FCSTD DOCUMENT  (FreeCAD 0.18R4 (GitTag))
Label: Ford_connector
License: All rights reserved
LicenseURL: http://en.wikipedia.org/wiki/All_rights_reserved
objects: Sketcher::SketchObject×1, TechDraw::DrawSVGTemplate×1, TechDraw::DrawViewPart×1, TechDraw::DrawPage×1
note: 1 computed .brp shape members not serialized (recipe doc carries the construction recipe); baked Part::Feature solids carry a one-line shape summary decoded from their .brp

FEATURE [Sketcher::SketchObject] Sketch
  sketch-geometry (120):
    g0: LineSegment StartX=1.5875 StartY=0 StartZ=0 EndX=138.112 EndY=0 EndZ=0
    g1: LineSegment StartX=139.7 StartY=-1.5875 StartZ=0 EndX=139.7 EndY=-163.512 EndZ=0
    g2: LineSegment StartX=138.112 StartY=-165.1 StartZ=0 EndX=1.5875 EndY=-165.1 EndZ=0
    g3: LineSegment StartX=0 StartY=-163.512 StartZ=0 EndX=0 EndY=-1.5875 EndZ=0
    g4: Circle CenterX=6.0198 CenterY=-8.636 CenterZ=0 NormalX=0 NormalY=0 NormalZ=1 AngleXU=0 Radius=3.175
    g5: Circle CenterX=133.68 CenterY=-8.636 CenterZ=0 NormalX=0 NormalY=0 NormalZ=1 AngleXU=0 Radius=3.175
    g6: GeomPoint X=2.8448 Y=-8.636 Z=0
    g7: GeomPoint X=6.0198 Y=-5.461 Z=0
    g8: GeomPoint X=136.855 Y=-8.636 Z=0
    g9: Circle CenterX=21.59 CenterY=-3.175 CenterZ=0 NormalX=0 NormalY=0 NormalZ=1 AngleXU=0 Radius=0.635
    g10: Circle CenterX=22.86 CenterY=-6.35 CenterZ=0 NormalX=0 NormalY=0 NormalZ=1 AngleXU=0 Radius=0.635
    g11: Circle CenterX=24.13 CenterY=-9.525 CenterZ=0 NormalX=0 NormalY=0 NormalZ=1 AngleXU=0 Radius=0.635
    g12: GeomPoint X=21.59 Y=-2.54 Z=0
    g13: GeomPoint X=22.225 Y=-3.175 Z=0
    g14: GeomPoint X=22.86 Y=-5.715 Z=0
    g15: GeomPoint X=22.225 Y=-6.35 Z=0
    g16: GeomPoint X=24.13 Y=-8.89 Z=0
    g17: GeomPoint X=23.495 Y=-9.525 Z=0
    g18: LineSegment StartX=21.59 StartY=-3.175 StartZ=0 EndX=25.908 EndY=-3.18045 EndZ=0
    g19: Circle CenterX=28.448 CenterY=-9.53045 CenterZ=0 NormalX=0 NormalY=0 NormalZ=1 AngleXU=0 Radius=0.635
    g20: Circle CenterX=27.1866 CenterY=-6.35545 CenterZ=0 NormalX=0 NormalY=0 NormalZ=1 AngleXU=0 Radius=0.635
    g21: Circle CenterX=25.908 CenterY=-3.18045 CenterZ=0 NormalX=0 NormalY=0 NormalZ=1 AngleXU=0 Radius=0.635
    g22: LineSegment [constr] StartX=24.13 StartY=-9.525 StartZ=0 EndX=28.448 EndY=-9.53045 EndZ=0
    g23: Circle CenterX=32.766 CenterY=-9.5359 CenterZ=0 NormalX=0 NormalY=0 NormalZ=1 AngleXU=0 Radius=0.635
    g24: Circle CenterX=31.5133 CenterY=-6.3609 CenterZ=0 NormalX=0 NormalY=0 NormalZ=1 AngleXU=0 Radius=0.635
    g25: Circle CenterX=30.2433 CenterY=-3.1859 CenterZ=0 NormalX=0 NormalY=0 NormalZ=1 AngleXU=0 Radius=0.635
    g26: LineSegment [constr] StartX=28.448 StartY=-9.53045 StartZ=0 EndX=32.766 EndY=-9.5359 EndZ=0
    g27: Circle CenterX=37.084 CenterY=-9.54134 CenterZ=0 NormalX=0 NormalY=0 NormalZ=1 AngleXU=0 Radius=0.635
    g28: Circle CenterX=35.8399 CenterY=-6.36634 CenterZ=0 NormalX=0 NormalY=0 NormalZ=1 AngleXU=0 Radius=0.635
    g29: Circle CenterX=34.5699 CenterY=-3.19134 CenterZ=0 NormalX=0 NormalY=0 NormalZ=1 AngleXU=0 Radius=0.635
    g30: LineSegment [constr] StartX=32.766 StartY=-9.5359 StartZ=0 EndX=37.084 EndY=-9.54134 EndZ=0
    g31: Circle CenterX=41.402 CenterY=-9.54679 CenterZ=0 NormalX=0 NormalY=0 NormalZ=1 AngleXU=0 Radius=0.635
    g32: Circle CenterX=40.1665 CenterY=-6.37179 CenterZ=0 NormalX=0 NormalY=0 NormalZ=1 AngleXU=0 Radius=0.635
    g33: Circle CenterX=38.8965 CenterY=-3.19679 CenterZ=0 NormalX=0 NormalY=0 NormalZ=1 AngleXU=0 Radius=0.635
    g34: LineSegment [constr] StartX=37.084 StartY=-9.54134 StartZ=0 EndX=41.402 EndY=-9.54679 EndZ=0
    g35: Circle CenterX=45.72 CenterY=-9.55224 CenterZ=0 NormalX=0 NormalY=0 NormalZ=1 AngleXU=0 Radius=0.635
    g36: Circle CenterX=44.4931 CenterY=-6.37724 CenterZ=0 NormalX=0 NormalY=0 NormalZ=1 AngleXU=0 Radius=0.635
    g37: Circle CenterX=43.2232 CenterY=-3.20224 CenterZ=0 NormalX=0 NormalY=0 NormalZ=1 AngleXU=0 Radius=0.635
    g38: LineSegment [constr] StartX=41.402 StartY=-9.54679 StartZ=0 EndX=45.72 EndY=-9.55224 EndZ=0
    g39: Circle CenterX=50.038 CenterY=-9.55769 CenterZ=0 NormalX=0 NormalY=0 NormalZ=1 AngleXU=0 Radius=0.635
    g40: Circle CenterX=48.8198 CenterY=-6.38269 CenterZ=0 NormalX=0 NormalY=0 NormalZ=1 AngleXU=0 Radius=0.635
    g41: Circle CenterX=47.5498 CenterY=-3.20769 CenterZ=0 NormalX=0 NormalY=0 NormalZ=1 AngleXU=0 Radius=0.635
    g42: LineSegment [constr] StartX=45.72 StartY=-9.55224 StartZ=0 EndX=50.038 EndY=-9.55769 EndZ=0
    g43: Circle CenterX=54.356 CenterY=-9.56314 CenterZ=0 NormalX=0 NormalY=0 NormalZ=1 AngleXU=0 Radius=0.635
    g44: Circle CenterX=53.1464 CenterY=-6.38814 CenterZ=0 NormalX=0 NormalY=0 NormalZ=1 AngleXU=0 Radius=0.635
    g45: Circle CenterX=51.8764 CenterY=-3.21314 CenterZ=0 NormalX=0 NormalY=0 NormalZ=1 AngleXU=0 Radius=0.635
    g46: LineSegment [constr] StartX=50.038 StartY=-9.55769 StartZ=0 EndX=54.356 EndY=-9.56314 EndZ=0
    g47: Circle CenterX=58.674 CenterY=-9.56858 CenterZ=0 NormalX=0 NormalY=0 NormalZ=1 AngleXU=0 Radius=0.635
    g48: Circle CenterX=57.473 CenterY=-6.39358 CenterZ=0 NormalX=0 NormalY=0 NormalZ=1 AngleXU=0 Radius=0.635
    g49: Circle CenterX=56.203 CenterY=-3.21858 CenterZ=0 NormalX=0 NormalY=0 NormalZ=1 AngleXU=0 Radius=0.635
    g50: LineSegment [constr] StartX=54.356 StartY=-9.56314 StartZ=0 EndX=58.674 EndY=-9.56858 EndZ=0
    g51: Circle CenterX=62.992 CenterY=-9.57403 CenterZ=0 NormalX=0 NormalY=0 NormalZ=1 AngleXU=0 Radius=0.635
    g52: Circle CenterX=61.7997 CenterY=-6.39903 CenterZ=0 NormalX=0 NormalY=0 NormalZ=1 AngleXU=0 Radius=0.635
    g53: Circle CenterX=60.5297 CenterY=-3.22403 CenterZ=0 NormalX=0 NormalY=0 NormalZ=1 AngleXU=0 Radius=0.635
    g54: LineSegment [constr] StartX=58.674 StartY=-9.56858 StartZ=0 EndX=62.992 EndY=-9.57403 EndZ=0
    g55: Circle CenterX=71.12 CenterY=-3.175 CenterZ=0 NormalX=0 NormalY=0 NormalZ=1 AngleXU=0 Radius=0.635
    g56: Circle CenterX=72.39 CenterY=-6.35 CenterZ=0 NormalX=0 NormalY=0 NormalZ=1 AngleXU=0 Radius=0.635
    g57: Circle CenterX=73.66 CenterY=-9.525 CenterZ=0 NormalX=0 NormalY=0 NormalZ=1 AngleXU=0 Radius=0.635
    g58: LineSegment StartX=21.59 StartY=-3.175 StartZ=0 EndX=21.59 EndY=-6.35 EndZ=0
    g59: LineSegment StartX=21.59 StartY=-6.35 StartZ=0 EndX=22.86 EndY=-6.35 EndZ=0
    g60: LineSegment StartX=22.86 StartY=-6.35 StartZ=0 EndX=22.86 EndY=-9.525 EndZ=0
    g61: LineSegment StartX=24.13 StartY=-9.525 StartZ=0 EndX=22.86 EndY=-9.525 EndZ=0
    g62: LineSegment StartX=72.39 StartY=-6.35 StartZ=0 EndX=71.12 EndY=-6.35 EndZ=0
    g63: LineSegment StartX=73.66 StartY=-9.525 StartZ=0 EndX=72.39 EndY=-9.525 EndZ=0
    g64: LineSegment StartX=71.12 StartY=-3.175 StartZ=0 EndX=75.438 EndY=-3.175 EndZ=0
    g65: Circle CenterX=77.978 CenterY=-9.525 CenterZ=0 NormalX=0 NormalY=0 NormalZ=1 AngleXU=0 Radius=0.635
    g66: Circle CenterX=76.708 CenterY=-6.35 CenterZ=0 NormalX=0 NormalY=0 NormalZ=1 AngleXU=0 Radius=0.635
    g67: Circle CenterX=75.438 CenterY=-3.175 CenterZ=0 NormalX=0 NormalY=0 NormalZ=1 AngleXU=0 Radius=0.635
    g68: LineSegment [constr] StartX=73.66 StartY=-9.525 StartZ=0 EndX=77.978 EndY=-9.525 EndZ=0
    g69: Circle CenterX=82.296 CenterY=-9.525 CenterZ=0 NormalX=0 NormalY=0 NormalZ=1 AngleXU=0 Radius=0.635
    g70: Circle CenterX=81.026 CenterY=-6.35 CenterZ=0 NormalX=0 NormalY=0 NormalZ=1 AngleXU=0 Radius=0.635
    g71: Circle CenterX=79.756 CenterY=-3.175 CenterZ=0 NormalX=0 NormalY=0 NormalZ=1 AngleXU=0 Radius=0.635
    g72: LineSegment [constr] StartX=77.978 StartY=-9.525 StartZ=0 EndX=82.296 EndY=-9.525 EndZ=0
    g73: Circle CenterX=86.614 CenterY=-9.525 CenterZ=0 NormalX=0 NormalY=0 NormalZ=1 AngleXU=0 Radius=0.635
    g74: Circle CenterX=85.344 CenterY=-6.35 CenterZ=0 NormalX=0 NormalY=0 NormalZ=1 AngleXU=0 Radius=0.635
    g75: Circle CenterX=84.074 CenterY=-3.175 CenterZ=0 NormalX=0 NormalY=0 NormalZ=1 AngleXU=0 Radius=0.635
    g76: LineSegment [constr] StartX=82.296 StartY=-9.525 StartZ=0 EndX=86.614 EndY=-9.525 EndZ=0
    g77: Circle CenterX=90.932 CenterY=-9.525 CenterZ=0 NormalX=0 NormalY=0 NormalZ=1 AngleXU=0 Radius=0.635
    g78: Circle CenterX=89.662 CenterY=-6.35 CenterZ=0 NormalX=0 NormalY=0 NormalZ=1 AngleXU=0 Radius=0.635
    g79: Circle CenterX=88.392 CenterY=-3.175 CenterZ=0 NormalX=0 NormalY=0 NormalZ=1 AngleXU=0 Radius=0.635
    g80: LineSegment [constr] StartX=86.614 StartY=-9.525 StartZ=0 EndX=90.932 EndY=-9.525 EndZ=0
    g81: Circle CenterX=95.25 CenterY=-9.525 CenterZ=0 NormalX=0 NormalY=0 NormalZ=1 AngleXU=0 Radius=0.635
    g82: Circle CenterX=93.98 CenterY=-6.35 CenterZ=0 NormalX=0 NormalY=0 NormalZ=1 AngleXU=0 Radius=0.635
    g83: Circle CenterX=92.71 CenterY=-3.175 CenterZ=0 NormalX=0 NormalY=0 NormalZ=1 AngleXU=0 Radius=0.635
    g84: LineSegment [constr] StartX=90.932 StartY=-9.525 StartZ=0 EndX=95.25 EndY=-9.525 EndZ=0
    g85: Circle CenterX=99.568 CenterY=-9.525 CenterZ=0 NormalX=0 NormalY=0 NormalZ=1 AngleXU=0 Radius=0.635
    g86: Circle CenterX=98.298 CenterY=-6.35 CenterZ=0 NormalX=0 NormalY=0 NormalZ=1 AngleXU=0 Radius=0.635
    g87: Circle CenterX=97.028 CenterY=-3.175 CenterZ=0 NormalX=0 NormalY=0 NormalZ=1 AngleXU=0 Radius=0.635
    g88: LineSegment [constr] StartX=95.25 StartY=-9.525 StartZ=0 EndX=99.568 EndY=-9.525 EndZ=0
    g89: Circle CenterX=103.886 CenterY=-9.525 CenterZ=0 NormalX=0 NormalY=0 NormalZ=1 AngleXU=0 Radius=0.635
    g90: Circle CenterX=102.616 CenterY=-6.35 CenterZ=0 NormalX=0 NormalY=0 NormalZ=1 AngleXU=0 Radius=0.635
    g91: Circle CenterX=101.346 CenterY=-3.175 CenterZ=0 NormalX=0 NormalY=0 NormalZ=1 AngleXU=0 Radius=0.635
    g92: LineSegment [constr] StartX=99.568 StartY=-9.525 StartZ=0 EndX=103.886 EndY=-9.525 EndZ=0
    g93: Circle CenterX=108.204 CenterY=-9.525 CenterZ=0 NormalX=0 NormalY=0 NormalZ=1 AngleXU=0 Radius=0.635
    g94: Circle CenterX=106.934 CenterY=-6.35 CenterZ=0 NormalX=0 NormalY=0 NormalZ=1 AngleXU=0 Radius=0.635
    g95: Circle CenterX=105.664 CenterY=-3.175 CenterZ=0 NormalX=0 NormalY=0 NormalZ=1 AngleXU=0 Radius=0.635
    g96: LineSegment [constr] StartX=103.886 StartY=-9.525 StartZ=0 EndX=108.204 EndY=-9.525 EndZ=0
    g97: Circle CenterX=112.522 CenterY=-9.525 CenterZ=0 NormalX=0 NormalY=0 NormalZ=1 AngleXU=0 Radius=0.635
    g98: Circle CenterX=111.252 CenterY=-6.35 CenterZ=0 NormalX=0 NormalY=0 NormalZ=1 AngleXU=0 Radius=0.635
    g99: Circle CenterX=109.982 CenterY=-3.175 CenterZ=0 NormalX=0 NormalY=0 NormalZ=1 AngleXU=0 Radius=0.635
    g100: LineSegment [constr] StartX=108.204 StartY=-9.525 StartZ=0 EndX=112.522 EndY=-9.525 EndZ=0
    g101: Circle CenterX=16.383 CenterY=-4.826 CenterZ=0 NormalX=0 NormalY=0 NormalZ=1 AngleXU=0 Radius=1.905
    g102: Circle CenterX=124.46 CenterY=-4.826 CenterZ=0 NormalX=0 NormalY=0 NormalZ=1 AngleXU=0 Radius=1.905
    g103: GeomPoint X=14.478 Y=-4.826 Z=0
    g104: GeomPoint X=16.383 Y=-2.921 Z=0
    g105: GeomPoint X=122.555 Y=-4.826 Z=0
    g106: ArcOfCircle CenterX=138.112 CenterY=-1.5875 CenterZ=0 NormalX=0 NormalY=0 NormalZ=1 AngleXU=0 Radius=1.5875 StartAngle=0 EndAngle=1.5708
    g107: ArcOfCircle CenterX=1.5875 CenterY=-1.5875 CenterZ=0 NormalX=0 NormalY=0 NormalZ=1 AngleXU=0 Radius=1.5875 StartAngle=1.5708 EndAngle=3.14159
    g108: ArcOfCircle CenterX=1.5875 CenterY=-163.512 CenterZ=0 NormalX=0 NormalY=0 NormalZ=1 AngleXU=0 Radius=1.5875 StartAngle=3.14159 EndAngle=4.71239
    g109: ArcOfCircle CenterX=138.112 CenterY=-163.512 CenterZ=0 NormalX=0 NormalY=0 NormalZ=1 AngleXU=0 Radius=1.5875 StartAngle=4.71239 EndAngle=6.28319
    g110: Circle CenterX=10.414 CenterY=-80.518 CenterZ=0 NormalX=0 NormalY=0 NormalZ=1 AngleXU=0 Radius=1.524
    g111: Circle CenterX=129.286 CenterY=-80.518 CenterZ=0 NormalX=0 NormalY=0 NormalZ=1 AngleXU=0 Radius=1.524
    g112: Circle CenterX=5.461 CenterY=-155.956 CenterZ=0 NormalX=0 NormalY=0 NormalZ=1 AngleXU=0 Radius=1.524
    g113: Circle CenterX=134.239 CenterY=-155.956 CenterZ=0 NormalX=0 NormalY=0 NormalZ=1 AngleXU=0 Radius=1.524
    g114: GeomPoint X=3.937 Y=-155.956 Z=0
    g115: GeomPoint X=5.461 Y=-157.48 Z=0
    g116: GeomPoint X=8.89 Y=-80.518 Z=0
    g117: GeomPoint X=10.414 Y=-82.042 Z=0
    g118: GeomPoint X=130.81 Y=-80.518 Z=0
    g119: GeomPoint X=135.763 Y=-155.956 Z=0
  constraints (271):
    c: Horizontal(g0)
    c: Horizontal(g2)
    c: Vertical(g1)
    c: Vertical(g3)
    c: Horizontal(g4,g5)
    c: Radius(g4) = 3.175
    c: Equal(g4,g5)
    c: PointOnObject(g6,g4)
    c: PointOnObject(g7,g4)
    c: PointOnObject(g8,g5)
    c: Horizontal(g5,g8)
    c: Horizontal(g6,g4)
    c: Vertical(g7,g4)
    c: DistanceX(g-1,g6) = 2.8448
    c: DistanceY(g7,g-1) = 5.461
    c: Equal(g9,g10)
    c: Equal(g10,g11)
    c: PointOnObject(g13,g9)
    c: PointOnObject(g14,g10)
    c: PointOnObject(g15,g10)
    c: PointOnObject(g17,g11)
    c: Horizontal(g11,g17)
    c: PointOnObject(g16,g11)
    c: Vertical(g11,g16)
    c: Horizontal(g10,g15)
    c: Vertical(g14,g10)
    c: Horizontal(g9,g13)
    c: DistanceX(g-1,g9) = 21.59
    c: DistanceX(g-1,g10) = 22.86
    c: DistanceX(g-1,g11) = 24.13
    c: DistanceY(g9,g-1) = 3.175
    c: DistanceY(g10,g9) = 3.175
    c: DistanceY(g11,g10) = 3.175
    c: Equal(g21,g20)
    c: Equal(g20,g19)
    c: Radius(g21) = 0.635
    c: DistanceY(g20,g21) = 3.175
    c: DistanceY(g19,g20) = 3.175
    c: Coincident(g11,g22)
    c: Coincident(g19,g22)
    c: Distance(g22) = 4.318
    c: Angle(g22) = -0.00126172
    c: Equal(g25,g24)
    c: Equal(g24,g23)
    c: Radius(g25) = 0.635
    c: DistanceY(g24,g25) = 3.175
    c: DistanceY(g23,g24) = 3.175
    c: Coincident(g19,g26)
    c: Coincident(g23,g26)
    c: Equal(g22,g26)
    c: Parallel(g26,g22)
    c: Equal(g29,g28)
    c: Equal(g28,g27)
    c: Radius(g29) = 0.635
    c: DistanceY(g28,g29) = 3.175
    c: DistanceY(g27,g28) = 3.175
    c: Coincident(g23,g30)
    c: Coincident(g27,g30)
    c: Equal(g22,g30)
    c: Parallel(g30,g22)
    c: Equal(g33,g32)
    c: Equal(g32,g31)
    c: Radius(g33) = 0.635
    c: DistanceY(g32,g33) = 3.175
    c: DistanceY(g31,g32) = 3.175
    c: Coincident(g27,g34)
    c: Coincident(g31,g34)
    c: Equal(g22,g34)
    c: Parallel(g34,g22)
    c: Equal(g37,g36)
    c: Equal(g36,g35)
    c: Radius(g37) = 0.635
    c: DistanceY(g36,g37) = 3.175
    c: DistanceY(g35,g36) = 3.175
    c: Coincident(g31,g38)
    c: Coincident(g35,g38)
    c: Equal(g22,g38)
    c: Parallel(g38,g22)
    c: Equal(g41,g40)
    c: Equal(g40,g39)
    c: Radius(g41) = 0.635
    c: DistanceY(g40,g41) = 3.175
    c: DistanceY(g39,g40) = 3.175
    c: Coincident(g35,g42)
    c: Coincident(g39,g42)
    c: Equal(g22,g42)
    c: Parallel(g42,g22)
    c: Equal(g45,g44)
    c: Equal(g44,g43)
    c: Radius(g45) = 0.635
    c: DistanceY(g44,g45) = 3.175
    c: DistanceY(g43,g44) = 3.175
    c: Coincident(g39,g46)
    c: Coincident(g43,g46)
    c: Equal(g22,g46)
    c: Parallel(g46,g22)
    c: Equal(g49,g48)
    c: Equal(g48,g47)
    c: Radius(g49) = 0.635
    c: DistanceY(g48,g49) = 3.175
    c: DistanceY(g47,g48) = 3.175
    c: Coincident(g43,g50)
    c: Coincident(g47,g50)
    c: Equal(g22,g50)
    c: Parallel(g50,g22)
    c: Equal(g53,g52)
    c: Equal(g52,g51)
    c: Radius(g53) = 0.635
    c: DistanceY(g52,g53) = 3.175
    c: DistanceY(g51,g52) = 3.175
    c: Coincident(g47,g54)
    c: Coincident(g51,g54)
    c: Equal(g22,g54)
    c: Parallel(g54,g22)
    c: DistanceX(g18,g18) = 4.318
    c: Equal(g55,g56)
    c: Equal(g56,g57)
    c: DistanceY(g56,g55) = 3.175
    c: DistanceY(g57,g56) = 3.175
    c: Coincident(g58,g9)
    c: Coincident(g59,g58)
    c: Coincident(g59,g10)
    c: Coincident(g60,g10)
    c: Coincident(g61,g11)
    c: Coincident(g61,g60)
    c: Vertical(g58)
    c: Vertical(g60)
    c: Horizontal(g61)
    c: Horizontal(g59)
    c: Coincident(g62,g56)
    c: Horizontal(g62)
    c: Coincident(g63,g57)
    c: Horizontal(g63)
    c: Equal(g63,g62)
    c: Equal(g63,g61)
    c: Vertical(g63,g56)
    c: Vertical(g62,g55)
    c: Coincident(g55,g64)
    c: DistanceX(g64,g64) = 4.318
    c: Equal(g55,g9)
    c: DistanceX(g-1,g55) = 71.12
    c: Radius(g9) = 0.635
    c: Coincident(g21,g18)
    c: Coincident(g9,g18)
    c: Equal(g67,g66)
    c: Equal(g66,g65)
    c: DistanceY(g66,g67) = 3.175
    c: DistanceY(g65,g66) = 3.175
    c: Coincident(g57,g68)
    c: Coincident(g65,g68)
    c: Distance(g68) = 4.318
    c: Angle(g68) = 0
    c: Equal(g71,g70)
    c: Equal(g70,g69)
    c: DistanceY(g70,g71) = 3.175
    c: DistanceY(g69,g70) = 3.175
    c: Coincident(g65,g72)
    c: Coincident(g69,g72)
    c: Equal(g68,g72)
    c: Parallel(g72,g68)
    c: Equal(g75,g74)
    c: Equal(g74,g73)
    c: DistanceY(g74,g75) = 3.175
    c: DistanceY(g73,g74) = 3.175
    c: Coincident(g69,g76)
    c: Coincident(g73,g76)
    c: Equal(g68,g76)
    c: Parallel(g76,g68)
    c: Equal(g79,g78)
    c: Equal(g78,g77)
    c: DistanceY(g78,g79) = 3.175
    c: DistanceY(g77,g78) = 3.175
    c: Coincident(g73,g80)
    c: Coincident(g77,g80)
    c: Equal(g68,g80)
    c: Parallel(g80,g68)
    c: Equal(g83,g82)
    c: Equal(g82,g81)
    c: DistanceY(g82,g83) = 3.175
    c: DistanceY(g81,g82) = 3.175
    c: Coincident(g77,g84)
    c: Coincident(g81,g84)
    c: Equal(g68,g84)
    c: Parallel(g84,g68)
    c: Equal(g87,g86)
    c: Equal(g86,g85)
    c: DistanceY(g86,g87) = 3.175
    c: DistanceY(g85,g86) = 3.175
    c: Coincident(g81,g88)
    c: Coincident(g85,g88)
    c: Equal(g68,g88)
    c: Parallel(g88,g68)
    c: Equal(g91,g90)
    c: Equal(g90,g89)
    c: DistanceY(g90,g91) = 3.175
    c: DistanceY(g89,g90) = 3.175
    c: Coincident(g85,g92)
    c: Coincident(g89,g92)
    c: Equal(g68,g92)
    c: Parallel(g92,g68)
    c: Equal(g95,g94)
    c: Equal(g94,g93)
    c: DistanceY(g94,g95) = 3.175
    c: DistanceY(g93,g94) = 3.175
    c: Coincident(g89,g96)
    c: Coincident(g93,g96)
    c: Equal(g68,g96)
    c: Parallel(g96,g68)
    c: Equal(g99,g98)
    c: Equal(g98,g97)
    c: DistanceY(g98,g99) = 3.175
    c: DistanceY(g97,g98) = 3.175
    c: Coincident(g93,g100)
    c: Coincident(g97,g100)
    c: Equal(g68,g100)
    c: Parallel(g100,g68)
    c: Coincident(g58,g64)
    c: Equal(g102,g101)
    c: Radius(g101) = 1.905
    c: PointOnObject(g103,g101)
    c: PointOnObject(g104,g101)
    c: Vertical(g101,g104)
    c: Horizontal(g103,g101)
    c: PointOnObject(g105,g102)
    c: Horizontal(g102,g105)
    c: Horizontal(g101,g102)
    c: DistanceY(g101,g-1) = 4.826
    c: DistanceX(g-1,g101) = 16.383
    c: DistanceX(g-1,g102) = 124.46
    c: Tangent(g0,g106) = 1.5708
    c: Tangent(g1,g106) = 1.5708
    c: Tangent(g3,g107) = 1.5708
    c: Tangent(g0,g107) = 1.5708
    c: Tangent(g2,g108) = 1.5708
    c: Tangent(g3,g108) = 1.5708
    c: Tangent(g2,g109) = 1.5708
    c: Tangent(g1,g109) = 1.5708
    c: Equal(g108,g109)
    c: Equal(g109,g106)
    c: Equal(g106,g107)
    c: Radius(g107) = 1.5875
    c: Horizontal(g0,g-1)
    c: Vertical(g3,g-1)
    c: DistanceX(g3,g1) = 139.7
    c: DistanceY(g2,g0) = 165.1
    c: Equal(g110,g111)
    c: Equal(g111,g113)
    c: Equal(g113,g112)
    c: Radius(g110) = 1.524
    c: Horizontal(g110,g111)
    c: Horizontal(g113,g112)
    c: PointOnObject(g114,g112)
    c: PointOnObject(g115,g112)
    c: PointOnObject(g116,g110)
    c: PointOnObject(g117,g110)
    c: PointOnObject(g118,g111)
    c: PointOnObject(g119,g113)
    c: Horizontal(g113,g119)
    c: Horizontal(g118,g111)
    c: Horizontal(g110,g116)
    c: Vertical(g117,g110)
    c: Vertical(g112,g115)
    c: Horizontal(g114,g112)
    c: DistanceX(g3,g114) = 3.937
    c: DistanceX(g119,g1) = 3.937
    c: DistanceX(g3,g116) = 8.89
    c: DistanceX(g118,g1) = 8.89
    c: DistanceY(g117,g0) = 82.042
    c: DistanceY(g115,g0) = 157.48
    c: Horizontal(g64)
    c: Horizontal(g64,g9)
FEATURE [TechDraw::DrawSVGTemplate] Template
  EditableTexts = Approved1=Approved 1; Approved2=Approved 2; CheckedBy=Checked By; Code=Code; CompanyAddress=1234 Main St; CompanyName=Company Name; DrawingNumber=Drawing Number; DrawingTitle1=Drawing Title 1; DrawingTitle2=Drawing Title 2; DrawingTitle3=Drawing Title 3; DrawnBy=Drawn By; Revision=Rev; Scale=Scale; Sheet=Sheet n of m; Weight=Weight
  Height = 279.4
  Orientation = 1
  Width = 431.8
FEATURE [TechDraw::DrawViewPart] View001
  CoarseView = false
  Direction = (0,0,1)
  Focus = 100
  HardHidden = false
  IsoCount = 0
  IsoHidden = false
  IsoVisible = false
  LockPosition = false
  Perspective = false
  Rotation = 0
  ScaleType = 0
  SeamHidden = false
  SeamVisible = false
  SmoothHidden = false
  SmoothVisible = false
  Source = -> [Sketch]
  X = 122.583
  Y = 140.804
FEATURE [TechDraw::DrawPage] Page001
  KeepUpdated = true
  ProjectionType = 0
  Template = -> Template
  Views = -> [View001]
